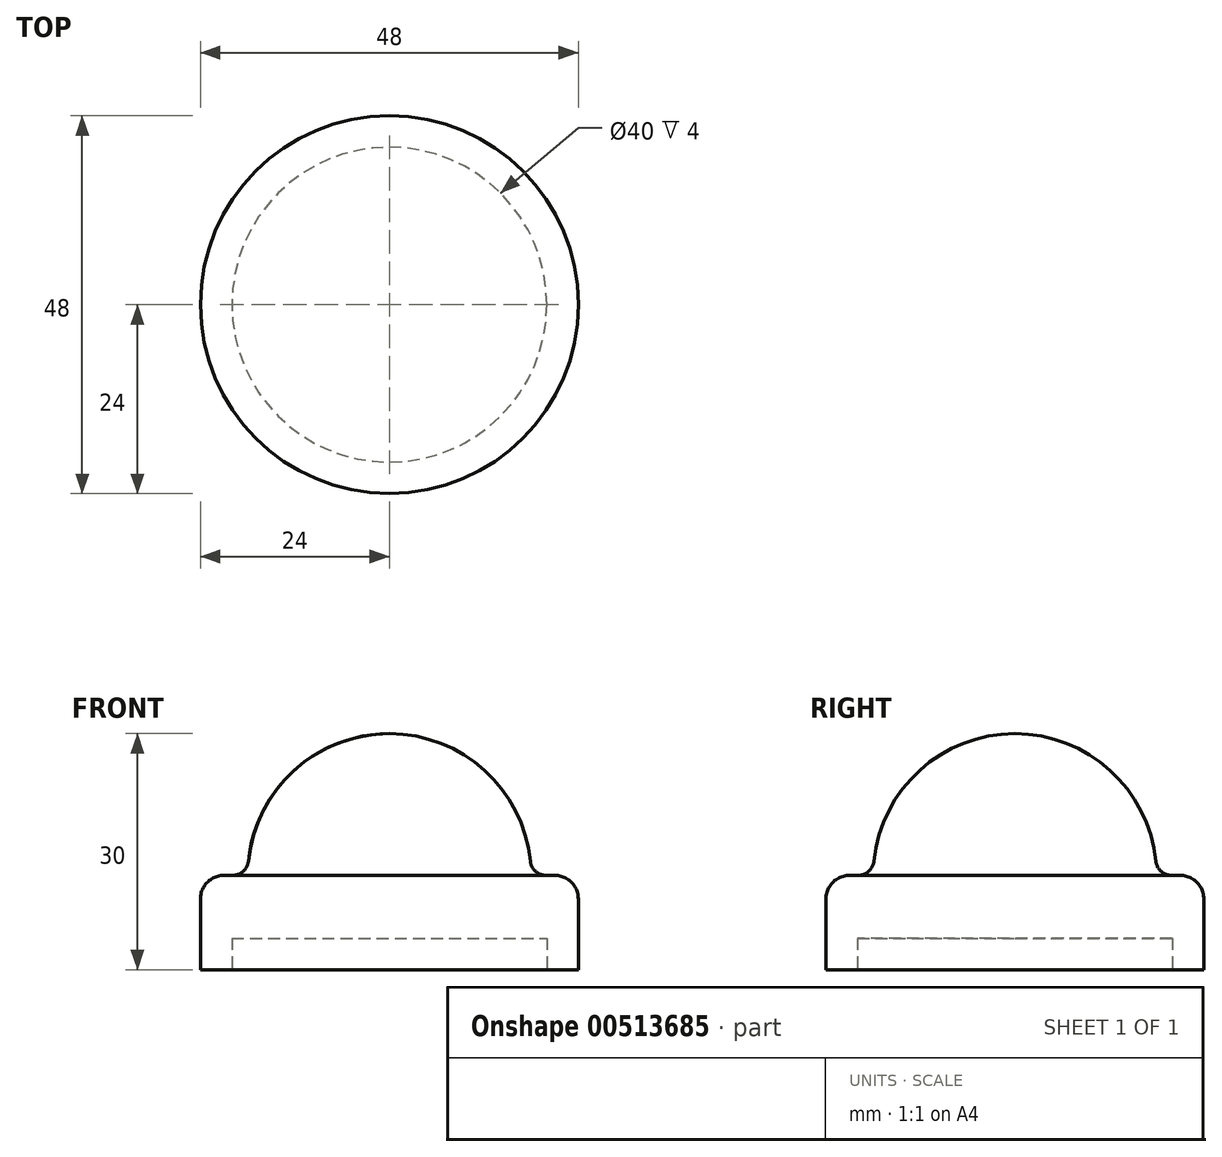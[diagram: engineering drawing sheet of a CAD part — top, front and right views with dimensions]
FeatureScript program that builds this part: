
annotation { "Feature Type Name" : "Feature", "Feature Type Description" : "" }
export const myFeature = defineFeature(function(context is Context, id is Id, definition is map)
    precondition{}
    {
        {
            var Q0;
            Q0=qCreatedBy(makeId("Front.planeOp"),FACE);
            var sketch = newSketch(context, id + "F0", { "sketchPlane" : qUnion([Q0])});
            skLineSegment(sketch, "E0", {"start": v(0, 0) * mm, "end": v(-20, 0) * mm});
            skLineSegment(sketch, "E1", {"start": v(-20, 0) * mm, "end": v(-20, -4) * mm});
            skLineSegment(sketch, "E2", {"start": v(-20, -4) * mm, "end": v(-24, -4) * mm});
            skLineSegment(sketch, "E3", {"start": v(-24, -4) * mm, "end": v(-24, 8) * mm});
            skLineSegment(sketch, "E4", {"start": v(-24, 8) * mm, "end": v(-18, 8) * mm});
            skLineSegment(sketch, "E5", {"start": v(0, 8) * mm, "end": v(0, 26) * mm});
            skArc(sketch, "E6", {"start": v(0, 26) * mm, "mid": v(-12.73, 20.73) * mm, "end": v(-18, 8) * mm});
            skLineSegment(sketch, "E7", {"start": v(0, 8) * mm, "end": v(0, 0) * mm});
            skSolve(sketch);
        }
        {
            var Q0;
            Q0=makeQuery(id+"F0.imprint","IMPRINT",FACE,{"disambiguationData":[TD([[makeQuery(id+"F0.imprint","IMPRINT",EDGE,{"derivedFrom":sQuery(id+"F0.wireOp",EDGE,"E0")}),-1.0]])]});
            var Q1;
            Q1=sQuery(id+"F0.wireOp",EDGE,"E5");
            revolve(context, id + "F1", {"entities" : qUnion([Q0]), "axis" : qUnion([Q1]), "revolveType" : RevolveType.FULL});
        }
        {
            var Q0;
            Q0=makeQuery(id+"F1.opRevolve","SWEPT_EDGE",EDGE,{"disambiguationData":[OSD([sQuery(id+"F0.wireOp",EDGE,"E4"),sQuery(id+"F0.wireOp",EDGE,"E6")])]});
            fillet(context, id + "F2", {"entities" : qUnion([Q0]), "radius" : 2 * mm, "tangentPropagation" : true, "allowEdgeOverflow" : false});
        }
        {
            var Q0;
            Q0=makeQuery(id+"F1.opRevolve","SWEPT_EDGE",EDGE,{"disambiguationData":[OSD([sQuery(id+"F0.wireOp",EDGE,"E3"),sQuery(id+"F0.wireOp",EDGE,"E4")])]});
            fillet(context, id + "F3", {"entities" : qUnion([Q0]), "radius" : 3 * mm, "tangentPropagation" : true, "allowEdgeOverflow" : false});
        }
    });
